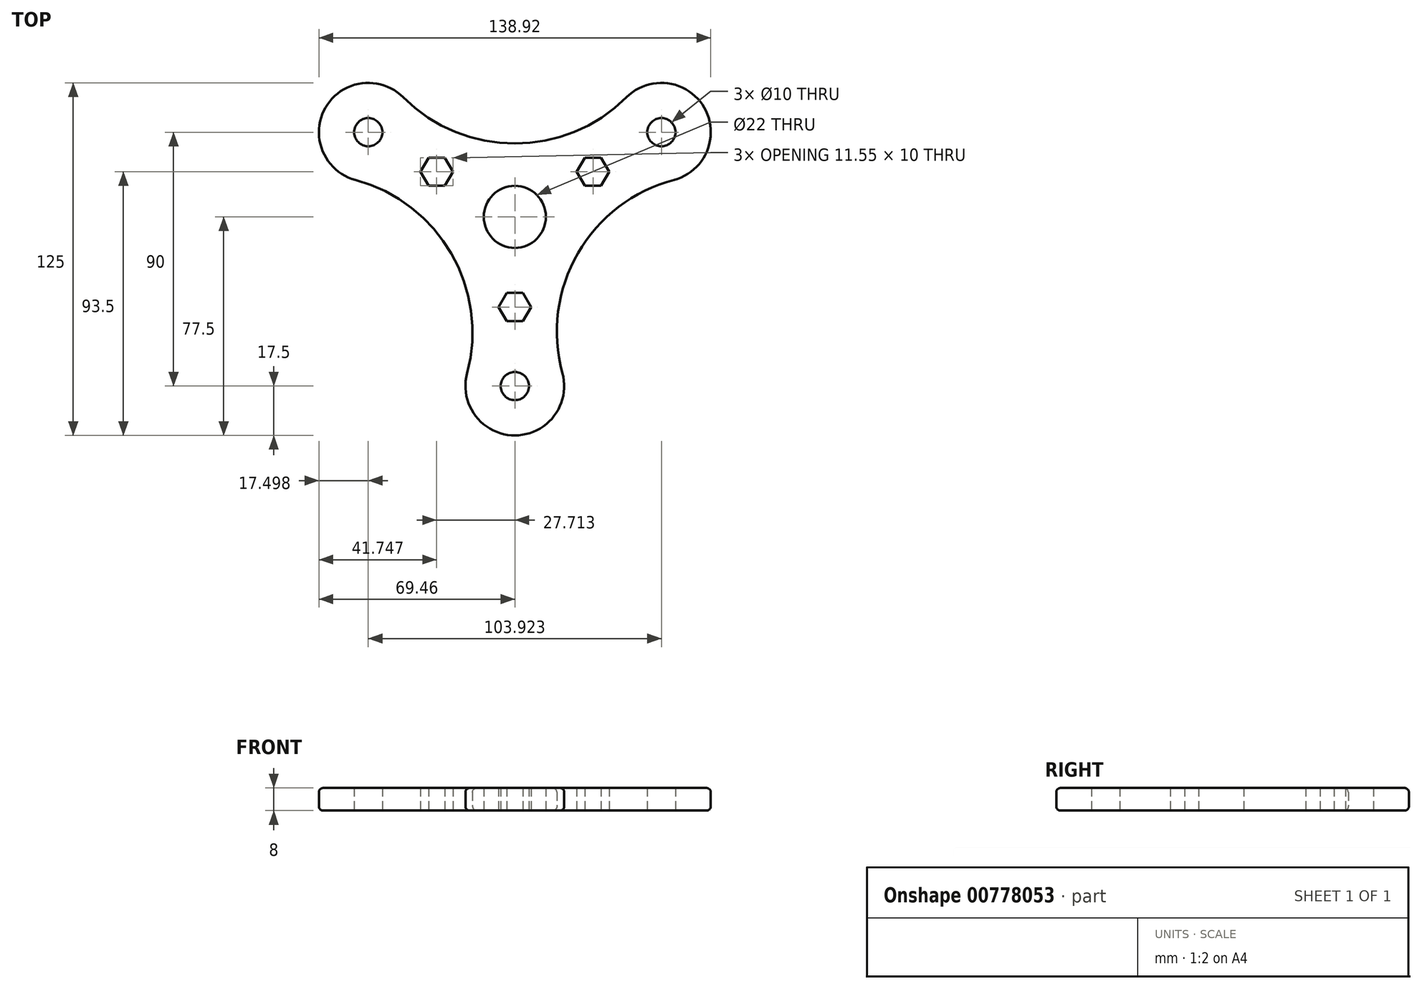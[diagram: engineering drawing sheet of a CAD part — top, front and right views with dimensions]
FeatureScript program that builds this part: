
annotation { "Feature Type Name" : "Feature", "Feature Type Description" : "" }
export const myFeature = defineFeature(function(context is Context, id is Id, definition is map)
    precondition{}
    {
        {
            var Q0;
            Q0=qCreatedBy(makeId("Top.planeOp"),FACE);
            var sketch = newSketch(context, id + "F0", { "sketchPlane" : qUnion([Q0])});
            skCircle(sketch, "E0", {"center": v(0, 0) * mm, "radius": 11 * mm});
            skCircle(sketch, "E1.cCircle", {"center": v(0, 0) * mm, "radius": 30 * mm, "construction": true});
            skLineSegment(sketch, "E1.0", {"start": v(-51.96, 30) * mm, "end": v(51.96, 30) * mm});
            skLineSegment(sketch, "E1.1", {"start": v(51.96, 30) * mm, "end": v(0, -60) * mm});
            skLineSegment(sketch, "E1.2", {"start": v(0, -60) * mm, "end": v(-51.96, 30) * mm});
            skPoint(sketch, "E1.0.midPoint", {"position": v(0, 30) * mm});
            skCircle(sketch, "E2", {"center": v(-51.96, 30) * mm, "radius": 17.5 * mm});
            skCircle(sketch, "E3", {"center": v(51.96, 30) * mm, "radius": 17.5 * mm});
            skCircle(sketch, "E4", {"center": v(0, -60) * mm, "radius": 17.5 * mm});
            skCircle(sketch, "E5", {"center": v(-51.96, 30) * mm, "radius": 5 * mm});
            skCircle(sketch, "E6", {"center": v(51.96, 30) * mm, "radius": 5 * mm});
            skCircle(sketch, "E7", {"center": v(0, -60) * mm, "radius": 5 * mm});
            skCircle(sketch, "E8.cCircle", {"center": v(0, 0) * mm, "radius": 16 * mm, "construction": true});
            skLineSegment(sketch, "E8.0", {"start": v(-27.71, 16) * mm, "end": v(27.71, 16) * mm, "construction": true});
            skLineSegment(sketch, "E8.1", {"start": v(27.71, 16) * mm, "end": v(0, -32) * mm, "construction": true});
            skLineSegment(sketch, "E8.2", {"start": v(0, -32) * mm, "end": v(-27.71, 16) * mm, "construction": true});
            skPoint(sketch, "E8.0.midPoint", {"position": v(0, 16) * mm});
            skLineSegment(sketch, "E9", {"start": v(0, 16) * mm, "end": v(0, 26) * mm, "construction": true});
            skLineSegment(sketch, "E10", {"start": v(-13.07, -9.37) * mm, "end": v(-21.73, -14.37) * mm, "construction": true});
            skLineSegment(sketch, "E11", {"start": v(16.16, -4) * mm, "end": v(24.82, -9) * mm, "construction": true});
            skArc(sketch, "E12", {"start": v(-39.6, 42.38) * mm, "mid": v(0, 26) * mm, "end": v(39.6, 42.38) * mm});
            skArc(sketch, "E13", {"start": v(-16.9, -55.47) * mm, "mid": v(-22.5, -12.99) * mm, "end": v(-56.5, 13.1) * mm});
            skArc(sketch, "E14", {"start": v(56.4, 13.07) * mm, "mid": v(22.35, -12.9) * mm, "end": v(16.88, -55.38) * mm});
            skCircle(sketch, "E15.cCircle", {"center": v(-27.71, 16) * mm, "radius": 5 * mm, "construction": true});
            skLineSegment(sketch, "E15.0", {"start": v(-21.94, 16) * mm, "end": v(-24.83, 11) * mm});
            skLineSegment(sketch, "E15.1", {"start": v(-24.83, 11) * mm, "end": v(-30.6, 11) * mm});
            skLineSegment(sketch, "E15.2", {"start": v(-30.6, 11) * mm, "end": v(-33.49, 16) * mm});
            skLineSegment(sketch, "E15.3", {"start": v(-33.49, 16) * mm, "end": v(-30.6, 21) * mm});
            skLineSegment(sketch, "E15.4", {"start": v(-30.6, 21) * mm, "end": v(-24.83, 21) * mm});
            skLineSegment(sketch, "E15.5", {"start": v(-24.83, 21) * mm, "end": v(-21.94, 16) * mm});
            skPoint(sketch, "E15.0.midPoint", {"position": v(-23.38, 13.5) * mm});
            skCircle(sketch, "E16.cCircle", {"center": v(0, -32) * mm, "radius": 5 * mm, "construction": true});
            skLineSegment(sketch, "E16.0", {"start": v(-2.89, -27) * mm, "end": v(2.89, -27) * mm});
            skLineSegment(sketch, "E16.1", {"start": v(2.89, -27) * mm, "end": v(5.77, -32) * mm});
            skLineSegment(sketch, "E16.2", {"start": v(5.77, -32) * mm, "end": v(2.89, -37) * mm});
            skLineSegment(sketch, "E16.3", {"start": v(2.89, -37) * mm, "end": v(-2.89, -37) * mm});
            skLineSegment(sketch, "E16.4", {"start": v(-2.89, -37) * mm, "end": v(-5.77, -32) * mm});
            skLineSegment(sketch, "E16.5", {"start": v(-5.77, -32) * mm, "end": v(-2.89, -27) * mm});
            skPoint(sketch, "E16.0.midPoint", {"position": v(0, -27) * mm});
            skCircle(sketch, "E17.cCircle", {"center": v(27.71, 16) * mm, "radius": 5 * mm, "construction": true});
            skLineSegment(sketch, "E17.0", {"start": v(24.83, 11) * mm, "end": v(21.94, 16) * mm});
            skLineSegment(sketch, "E17.1", {"start": v(21.94, 16) * mm, "end": v(24.83, 21) * mm});
            skLineSegment(sketch, "E17.2", {"start": v(24.83, 21) * mm, "end": v(30.6, 21) * mm});
            skLineSegment(sketch, "E17.3", {"start": v(30.6, 21) * mm, "end": v(33.49, 16) * mm});
            skLineSegment(sketch, "E17.4", {"start": v(33.49, 16) * mm, "end": v(30.6, 11) * mm});
            skLineSegment(sketch, "E17.5", {"start": v(30.6, 11) * mm, "end": v(24.83, 11) * mm});
            skPoint(sketch, "E17.0.midPoint", {"position": v(23.38, 13.5) * mm});
            skSolve(sketch);
        }
        {
            var Q0;
            {var subQ3=sQuery(id+"F0.wireOp",EDGE,"E5");var subQ4=sQuery(id+"F0.wireOp",EDGE,"E1.0");var subQ5=makeQuery(id+"F0.imprint","INTERSECT",VERTEX,{"derivedFrom":[subQ4,subQ3]});Q0=makeQuery(id+"F0.imprint","IMPRINT",FACE,{"disambiguationData":[TD([[makeQuery(id+"F0.imprint","IMPRINT",EDGE,{"disambiguationData":[TD([[subQ5,-1.0]])],"derivedFrom":subQ4}),1.0]])]});}
            var Q1;
            {var subQ0=sQuery(id+"F0.wireOp",EDGE,"E5");var subQ1=sQuery(id+"F0.wireOp",EDGE,"E1.0");var subQ2=makeQuery(id+"F0.imprint","INTERSECT",VERTEX,{"derivedFrom":[subQ1,subQ0]});Q1=makeQuery(id+"F0.imprint","IMPRINT",FACE,{"disambiguationData":[TD([[makeQuery(id+"F0.imprint","IMPRINT",EDGE,{"disambiguationData":[TD([[subQ2,-1.0]])],"derivedFrom":subQ1}),-1.0]])]});}
            var Q2;
            {var subQ0=sQuery(id+"F0.wireOp",EDGE,"E12");var subQ1=sQuery(id+"F0.wireOp",EDGE,"E1.0");var subQ2=makeQuery(id+"F0.imprint","INTERSECT",VERTEX,{"disambiguationData":[OD(0.0)],"derivedFrom":[subQ1,subQ0]});Q2=makeQuery(id+"F0.imprint","IMPRINT",FACE,{"disambiguationData":[TD([[makeQuery(id+"F0.imprint","IMPRINT",EDGE,{"disambiguationData":[TD([[subQ2,1.0]])],"derivedFrom":subQ1}),1.0]])]});}
            var Q3;
            {var subQ0=sQuery(id+"F0.wireOp",EDGE,"E13");var subQ1=sQuery(id+"F0.wireOp",EDGE,"E1.2");var subQ2=makeQuery(id+"F0.imprint","INTERSECT",VERTEX,{"disambiguationData":[OD(1.0)],"derivedFrom":[subQ1,subQ0]});Q3=makeQuery(id+"F0.imprint","IMPRINT",FACE,{"disambiguationData":[TD([[makeQuery(id+"F0.imprint","IMPRINT",EDGE,{"disambiguationData":[TD([[subQ2,-1.0]])],"derivedFrom":subQ1}),1.0]])]});}
            var Q4;
            {var subQ0=sQuery(id+"F0.wireOp",EDGE,"E4");var subQ5=sQuery(id+"F0.wireOp",EDGE,"E1.1");var subQ6=makeQuery(id+"F0.imprint","INTERSECT",VERTEX,{"derivedFrom":[subQ5,subQ0]});Q4=makeQuery(id+"F0.imprint","IMPRINT",FACE,{"disambiguationData":[TD([[makeQuery(id+"F0.imprint","IMPRINT",EDGE,{"disambiguationData":[TD([[subQ6,-1.0]])],"derivedFrom":subQ5}),1.0]])]});}
            var Q5;
            {var subQ0=sQuery(id+"F0.wireOp",EDGE,"E13");var subQ1=sQuery(id+"F0.wireOp",EDGE,"E1.2");var subQ2=makeQuery(id+"F0.imprint","INTERSECT",VERTEX,{"disambiguationData":[OD(0.0)],"derivedFrom":[subQ1,subQ0]});Q5=makeQuery(id+"F0.imprint","IMPRINT",FACE,{"disambiguationData":[TD([[makeQuery(id+"F0.imprint","IMPRINT",EDGE,{"disambiguationData":[TD([[subQ2,1.0]])],"derivedFrom":subQ1}),1.0]])]});}
            var Q6;
            {var subQ0=sQuery(id+"F0.wireOp",EDGE,"E4");var subQ1=sQuery(id+"F0.wireOp",EDGE,"E1.1");var subQ2=makeQuery(id+"F0.imprint","INTERSECT",VERTEX,{"derivedFrom":[subQ1,subQ0]});Q6=makeQuery(id+"F0.imprint","IMPRINT",FACE,{"disambiguationData":[TD([[makeQuery(id+"F0.imprint","IMPRINT",EDGE,{"disambiguationData":[TD([[subQ2,-1.0]])],"derivedFrom":subQ1}),-1.0]])]});}
            var Q7;
            {var subQ0=sQuery(id+"F0.wireOp",EDGE,"E14");var subQ1=sQuery(id+"F0.wireOp",EDGE,"E1.1");var subQ2=makeQuery(id+"F0.imprint","INTERSECT",VERTEX,{"disambiguationData":[OD(1.0)],"derivedFrom":[subQ1,subQ0]});Q7=makeQuery(id+"F0.imprint","IMPRINT",FACE,{"disambiguationData":[TD([[makeQuery(id+"F0.imprint","IMPRINT",EDGE,{"disambiguationData":[TD([[subQ2,-1.0]])],"derivedFrom":subQ1}),1.0]])]});}
            var Q8;
            Q8=makeQuery(id+"F0.imprint","IMPRINT",FACE,{"disambiguationData":[TD([[makeQuery(id+"F0.imprint","IMPRINT",EDGE,{"derivedFrom":sQuery(id+"F0.wireOp",EDGE,"E0")}),-1.0]])]});
            var Q9;
            {var subQ0=sQuery(id+"F0.wireOp",EDGE,"E3");var subQ1=sQuery(id+"F0.wireOp",EDGE,"E1.0");var subQ2=makeQuery(id+"F0.imprint","INTERSECT",VERTEX,{"derivedFrom":[subQ1,subQ0]});Q9=makeQuery(id+"F0.imprint","IMPRINT",FACE,{"disambiguationData":[TD([[makeQuery(id+"F0.imprint","IMPRINT",EDGE,{"disambiguationData":[TD([[subQ2,-1.0]])],"derivedFrom":subQ1}),-1.0]])]});}
            var Q10;
            {var subQ0=sQuery(id+"F0.wireOp",EDGE,"E14");var subQ1=sQuery(id+"F0.wireOp",EDGE,"E1.1");var subQ2=makeQuery(id+"F0.imprint","INTERSECT",VERTEX,{"disambiguationData":[OD(0.0)],"derivedFrom":[subQ1,subQ0]});Q10=makeQuery(id+"F0.imprint","IMPRINT",FACE,{"disambiguationData":[TD([[makeQuery(id+"F0.imprint","IMPRINT",EDGE,{"disambiguationData":[TD([[subQ2,1.0]])],"derivedFrom":subQ1}),1.0]])]});}
            var Q11;
            {var subQ0=sQuery(id+"F0.wireOp",EDGE,"E3");var subQ4=sQuery(id+"F0.wireOp",EDGE,"E1.0");var subQ5=makeQuery(id+"F0.imprint","INTERSECT",VERTEX,{"derivedFrom":[subQ4,subQ0]});Q11=makeQuery(id+"F0.imprint","IMPRINT",FACE,{"disambiguationData":[TD([[makeQuery(id+"F0.imprint","IMPRINT",EDGE,{"disambiguationData":[TD([[subQ5,-1.0]])],"derivedFrom":subQ4}),1.0]])]});}
            var Q12;
            {var subQ0=sQuery(id+"F0.wireOp",EDGE,"E12");var subQ1=sQuery(id+"F0.wireOp",EDGE,"E1.0");var subQ2=makeQuery(id+"F0.imprint","INTERSECT",VERTEX,{"disambiguationData":[OD(1.0)],"derivedFrom":[subQ1,subQ0]});Q12=makeQuery(id+"F0.imprint","IMPRINT",FACE,{"disambiguationData":[TD([[makeQuery(id+"F0.imprint","IMPRINT",EDGE,{"disambiguationData":[TD([[subQ2,-1.0]])],"derivedFrom":subQ1}),1.0]])]});}
            extrude(context, id + "F1", {"entities" : qUnion([Q0, Q1, Q2, Q3, Q4, Q5, Q6, Q7, Q8, Q9, Q10, Q11, Q12]), "endBound" : BoundingType.SYMMETRIC, "depth" : 8 * mm, "offsetDistance" : 25 * mm});
        }
        {
            var Q0;
            Q0=makeQuery(id+"F1.opExtrude","CAP_EDGE",EDGE,{"disambiguationData":[OSD([sQuery(id+"F0.wireOp",EDGE,"E13")])],"isStart":false});
            var Q1;
            Q1=makeQuery(id+"F1.opExtrude","CAP_EDGE",EDGE,{"disambiguationData":[OSD([sQuery(id+"F0.wireOp",EDGE,"E13")])],"isStart":true});
            fillet(context, id + "F2", {"entities" : qUnion([Q0, Q1]), "radius" : 1.5 * mm, "tangentPropagation" : true, "allowEdgeOverflow" : false});
        }
    });
